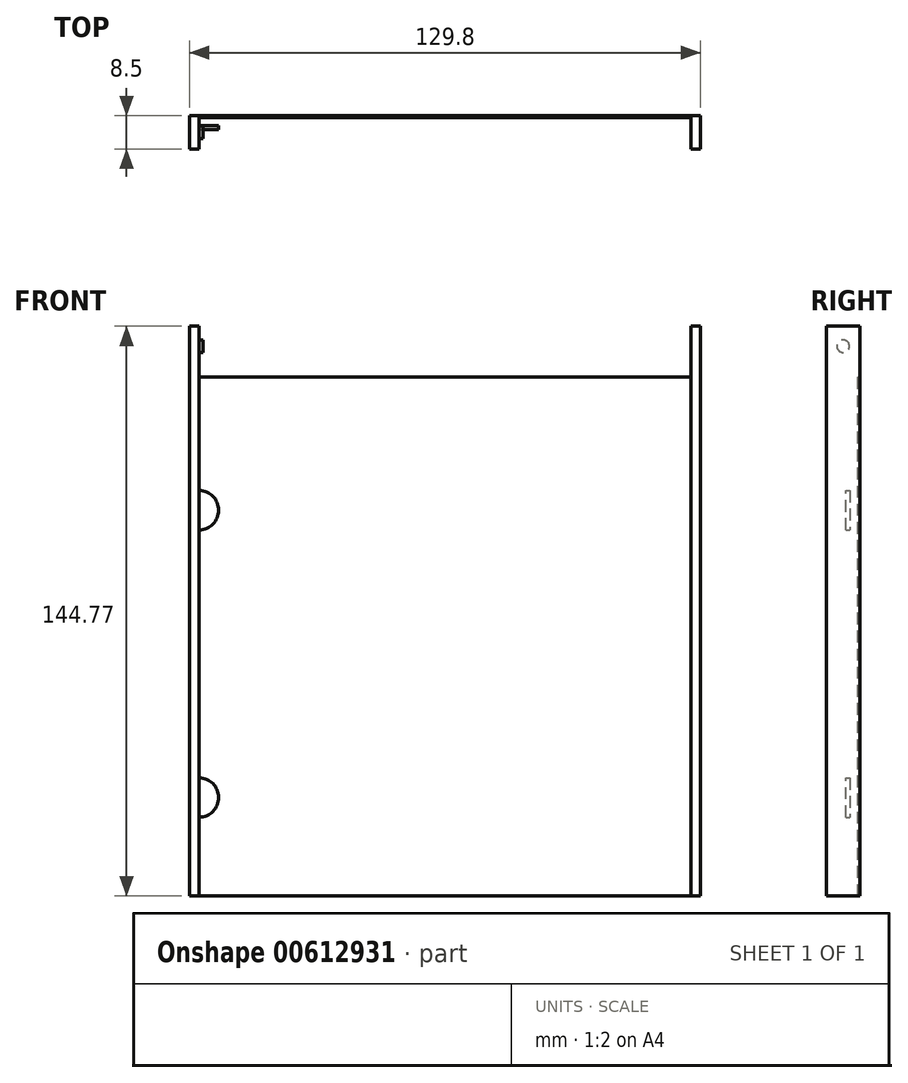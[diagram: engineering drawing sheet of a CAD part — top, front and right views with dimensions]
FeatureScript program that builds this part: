
annotation { "Feature Type Name" : "Feature", "Feature Type Description" : "" }
export const myFeature = defineFeature(function(context is Context, id is Id, definition is map)
    precondition{}
    {
        {
            var Q0;
            Q0=qCreatedBy(makeId("Front.planeOp"),FACE);
            var sketch = newSketch(context, id + "F0", { "sketchPlane" : qUnion([Q0])});
            skLineSegment(sketch, "E0.bottom", {"start": v(-64.9, -65.94) * mm, "end": v(64.9, -65.94) * mm});
            skLineSegment(sketch, "E0.top", {"start": v(-64.9, 65.94) * mm, "end": v(64.9, 65.94) * mm});
            skLineSegment(sketch, "E0.left", {"start": v(-64.9, -65.94) * mm, "end": v(-64.9, 65.94) * mm});
            skLineSegment(sketch, "E0.right", {"start": v(64.9, -65.94) * mm, "end": v(64.9, 65.94) * mm});
            skPoint(sketch, "E0.middle", {"position": v(0, 0) * mm});
            skLineSegment(sketch, "E1.0", {"start": v(-63.7, -65.94) * mm, "end": v(-63.7, 76.33) * mm});
            skLineSegment(sketch, "E2.0", {"start": v(63.7, -65.94) * mm, "end": v(63.7, 76.33) * mm});
            skSolve(sketch);
        }
        {
            var Q0;
            Q0 = qSketchRegion(id + "F0", true);
            var Q1;
            Q1=sQuery(id+"F0.wireOp",EDGE,"E0.left");
            var Q2;
            Q2=sQuery(id+"F0.wireOp",EDGE,"E0.right");
            extrude(context, id + "F1", {"entities" : qUnion([Q0]), "surfaceEntities" : qUnion([Q1, Q2]), "depth" : 8.5 * mm, "offsetDistance" : 25 * mm});
        }
        {
            var Q0;
            Q0=makeQuery(id+"F1.opExtrude","CAP_FACE",FACE,{"disambiguationData":[OSD([sQuery(id+"F0.wireOp",EDGE,"E0.bottom"),sQuery(id+"F0.wireOp",EDGE,"E0.top"),sQuery(id+"F0.wireOp",EDGE,"E0.left"),sQuery(id+"F0.wireOp",EDGE,"E0.right")])],"isStart":false});
            var sketch = newSketch(context, id + "F2", { "sketchPlane" : qUnion([Q0])});
            skLineSegment(sketch, "E3.bottom", {"start": v(62.5, -65.94) * mm, "end": v(-62.5, -65.94) * mm});
            skLineSegment(sketch, "E3.top", {"start": v(62.5, 65.94) * mm, "end": v(-62.5, 65.94) * mm});
            skLineSegment(sketch, "E3.left", {"start": v(62.5, -65.94) * mm, "end": v(62.5, 65.94) * mm});
            skLineSegment(sketch, "E3.right", {"start": v(-62.5, -65.94) * mm, "end": v(-62.5, 65.94) * mm});
            skPoint(sketch, "E3.middle", {"position": v(0, 0) * mm});
            skSolve(sketch);
        }
        {
            var Q0;
            Q0 = qSketchRegion(id + "F2", true);
            extrude(context, id + "F3", {"entities" : qUnion([Q0]), "operationType" : NewBodyOperationType.REMOVE, "oppositeDirection" : true, "depth" : 8 * mm, "offsetDistance" : 25 * mm});
        }
        {
            var Q0;
            Q0=makeQuery(id+"F1.opExtrude","SWEPT_FACE",FACE,{"disambiguationData":[OSD([sQuery(id+"F0.wireOp",EDGE,"E0.top")])]});
            var sketch = newSketch(context, id + "F4", { "sketchPlane" : qUnion([Q0])});
            skLineSegment(sketch, "E4.bottom", {"start": v(-62.5, -8.5) * mm, "end": v(-64.9, -8.5) * mm});
            skLineSegment(sketch, "E4.top", {"start": v(-62.5, 0) * mm, "end": v(-64.9, 0) * mm});
            skLineSegment(sketch, "E4.left", {"start": v(-62.5, -8.5) * mm, "end": v(-62.5, 0) * mm});
            skLineSegment(sketch, "E4.right", {"start": v(-64.9, -8.5) * mm, "end": v(-64.9, 0) * mm});
            skLineSegment(sketch, "E5.bottom", {"start": v(64.9, -8.5) * mm, "end": v(62.5, -8.5) * mm});
            skLineSegment(sketch, "E5.top", {"start": v(64.9, 0) * mm, "end": v(62.5, 0) * mm});
            skLineSegment(sketch, "E5.left", {"start": v(64.9, -8.5) * mm, "end": v(64.9, 0) * mm});
            skLineSegment(sketch, "E5.right", {"start": v(62.5, -8.5) * mm, "end": v(62.5, 0) * mm});
            skSolve(sketch);
        }
        {
            var Q0;
            Q0 = qSketchRegion(id + "F4", true);
            extrude(context, id + "F5", {"entities" : qUnion([Q0]), "operationType" : NewBodyOperationType.ADD, "depth" : 12.9 * mm, "offsetDistance" : 25 * mm});
        }
        {
            var Q0;
            Q0=makeQuery(id+"F5.boolean.opBoolean","MERGE",FACE,{"derivedFrom":[makeQuery(id+"F3.boolean.opBoolean","COPY",FACE,{"derivedFrom":makeQuery(id+"F3.opExtrude","SWEPT_FACE",FACE,{"disambiguationData":[OSD([sQuery(id+"F2.wireOp",EDGE,"E3.right")])]})}),makeQuery(id+"F5.opExtrude","SWEPT_FACE",FACE,{"disambiguationData":[OSD([sQuery(id+"F4.wireOp",EDGE,"E4.left")])]})]});
            var sketch = newSketch(context, id + "F6", { "sketchPlane" : qUnion([Q0])});
            skPoint(sketch, "E6.endSnap0", {"position": v(-4.25, 78.84) * mm});
            skLineSegment(sketch, "E7", {"start": v(-4.25, 78.84) * mm, "end": v(-4.25, 78.79) * mm, "construction": true});
            skCircle(sketch, "E8", {"center": v(-4.25, 73.73) * mm, "radius": 1.6 * mm});
            skSolve(sketch);
        }
        {
            var Q0;
            Q0=makeQuery(id+"F6.imprint","IMPRINT",FACE,{"disambiguationData":[TD([[makeQuery(id+"F6.imprint","IMPRINT",EDGE,{"derivedFrom":sQuery(id+"F6.wireOp",EDGE,"E8")}),1.0]])]});
            extrude(context, id + "F7", {"entities" : qUnion([Q0]), "operationType" : NewBodyOperationType.ADD, "depth" : 1 * mm, "offsetDistance" : 25 * mm});
        }
        {
            var Q0;
            Q0=makeQuery(id+"F3.boolean.opBoolean","COPY",FACE,{"derivedFrom":makeQuery(id+"F3.opExtrude","CAP_FACE",FACE,{"disambiguationData":[OSD([sQuery(id+"F2.wireOp",EDGE,"E3.bottom"),sQuery(id+"F2.wireOp",EDGE,"E3.top"),sQuery(id+"F2.wireOp",EDGE,"E3.left"),sQuery(id+"F2.wireOp",EDGE,"E3.right")])],"isStart":false})});
            var sketch = newSketch(context, id + "F8", { "sketchPlane" : qUnion([Q0])});
            skArc(sketch, "E9", {"start": v(-62.5, -45.93) * mm, "mid": v(-57.5, -40.94) * mm, "end": v(-62.5, -35.94) * mm});
            skLineSegment(sketch, "E10", {"start": v(-62.5, -35.94) * mm, "end": v(-62.5, -45.94) * mm});
            skArc(sketch, "E11.0.1.0", {"start": v(-62.5, 27.06) * mm, "mid": v(-57.5, 32.06) * mm, "end": v(-62.5, 37.06) * mm});
            skLineSegment(sketch, "E11.direction1", {"start": v(-62.5, -45.93) * mm, "end": v(-87.5, -45.93) * mm, "construction": true});
            skLineSegment(sketch, "E11.direction2", {"start": v(-62.5, -45.93) * mm, "end": v(-62.5, 27.06) * mm, "construction": true});
            skSolve(sketch);
        }
        {
            var Q0;
            Q0=makeQuery(id+"F8.imprint","IMPRINT",FACE,{"disambiguationData":[TD([[makeQuery(id+"F8.imprint","IMPRINT",EDGE,{"derivedFrom":sQuery(id+"F8.wireOp",EDGE,"E9")}),1.0]])]});
            var Q1;
            {var subQ0=sQuery(id+"F8.wireOp",EDGE,"E11.0.1.0");Q1=makeQuery(id+"F8.imprint","IMPRINT",FACE,{"disambiguationData":[TD([[makeQuery(id+"F8.imprint","IMPRINT",EDGE,{"derivedFrom":subQ0}),1.0]])]});}
            var Q2;
            Q2 = qConstructionFilter(qBodyType(qCreatedBy(id + "F8" ,EDGE), BodyType.WIRE), ConstructionObject.NO);
            extrude(context, id + "F9", {"entities" : qUnion([Q0, Q1]), "operationType" : NewBodyOperationType.ADD, "surfaceEntities" : qUnion([Q2]), "depth" : 3 * mm, "offsetDistance" : 25 * mm});
        }
        {
            var Q0;
            Q0=makeQuery(id+"F1.opExtrude","SWEPT_FACE",FACE,{"disambiguationData":[OSD([sQuery(id+"F0.wireOp",EDGE,"E0.bottom")])]});
            var sketch = newSketch(context, id + "F10", { "sketchPlane" : qUnion([Q0])});
            skLineSegment(sketch, "E12.bottom", {"start": v(-62.5, 0.5) * mm, "end": v(62.5, 0.5) * mm});
            skLineSegment(sketch, "E12.top", {"start": v(-62.5, 2.5) * mm, "end": v(62.5, 2.5) * mm});
            skLineSegment(sketch, "E12.left", {"start": v(-62.5, 0.5) * mm, "end": v(-62.5, 2.5) * mm});
            skLineSegment(sketch, "E12.right", {"start": v(62.5, 0.5) * mm, "end": v(62.5, 2.5) * mm});
            skSolve(sketch);
        }
        {
            var Q0;
            Q0 = qSketchRegion(id + "F10", true);
            extrude(context, id + "F11", {"entities" : qUnion([Q0]), "operationType" : NewBodyOperationType.REMOVE, "oppositeDirection" : true, "depth" : 130 * mm, "offsetDistance" : 25 * mm});
        }
    });
